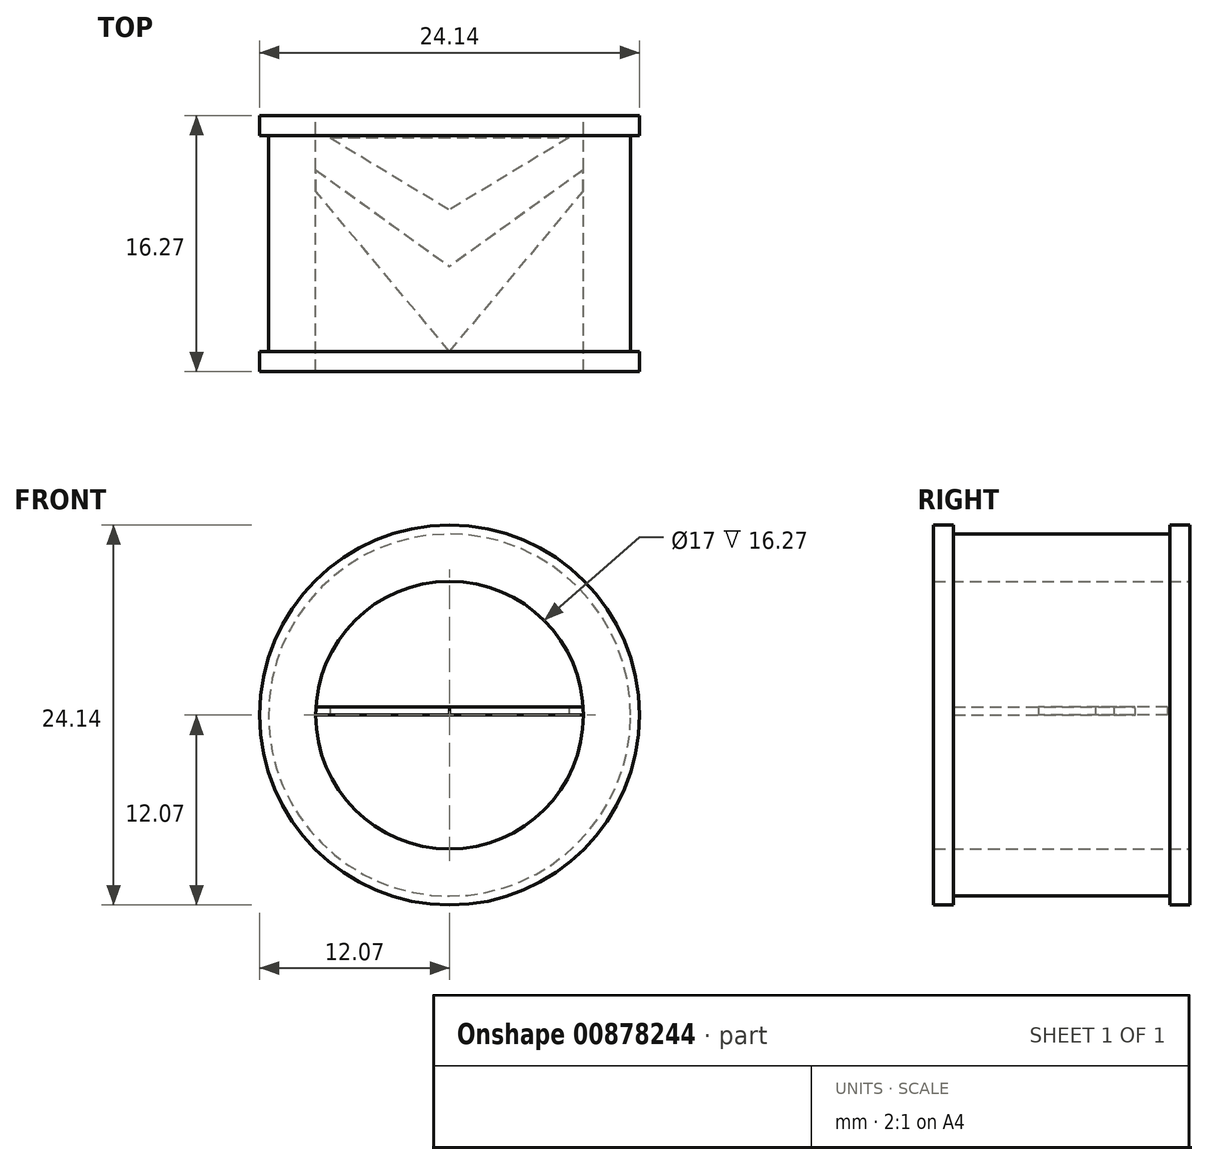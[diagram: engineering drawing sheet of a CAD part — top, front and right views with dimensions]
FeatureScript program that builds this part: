
annotation { "Feature Type Name" : "Feature", "Feature Type Description" : "" }
export const myFeature = defineFeature(function(context is Context, id is Id, definition is map)
    precondition{}
    {
        {
            var Q0;
            Q0=qCreatedBy(makeId("Front.planeOp"),FACE);
            var sketch = newSketch(context, id + "F0", { "sketchPlane" : qUnion([Q0])});
            skCircle(sketch, "E0", {"center": v(0, 0) * mm, "radius": 8.5 * mm});
            skCircle(sketch, "E1", {"center": v(0, 0) * mm, "radius": 11.5 * mm});
            skSolve(sketch);
        }
        {
            var Q0;
            Q0 = qSketchRegion(id + "F0", true);
            extrude(context, id + "F1", {"entities" : qUnion([Q0]), "depth" : 15 * mm, "offsetDistance" : 25.4 * mm});
        }
        {
            var Q0;
            Q0=qCreatedBy(makeId("Front.planeOp"),FACE);
            var sketch = newSketch(context, id + "F2", { "sketchPlane" : qUnion([Q0])});
            skCircle(sketch, "E2", {"center": v(0, 0) * mm, "radius": 12.07 * mm});
            skCircle(sketch, "E3", {"center": v(0, 0) * mm, "radius": 8.57 * mm});
            skSolve(sketch);
        }
        {
            var Q0;
            Q0=makeQuery(id+"F1.opExtrude","CAP_FACE",FACE,{"disambiguationData":[OSD([sQuery(id+"F0.wireOp",EDGE,"E0"),sQuery(id+"F0.wireOp",EDGE,"E1")])],"isStart":false});
            var Q1;
            Q1 = qSketchRegion(id + "F2", true);
            var Q2;
            Q2=sQuery(id+"F2.wireOp",EDGE,"E2");
            extrude(context, id + "F3", {"entities" : qUnion([Q0, Q1]), "operationType" : NewBodyOperationType.ADD, "surfaceOperationType" : NewSurfaceOperationType.ADD, "surfaceEntities" : qUnion([Q2]), "depth" : 1.27 * mm, "offsetDistance" : 25.4 * mm});
        }
        {
            var Q0;
            Q0=makeQuery(id+"F3.opExtrude","CAP_FACE",FACE,{"disambiguationData":[OSD([sQuery(id+"F0.wireOp",EDGE,"E0"),sQuery(id+"F0.wireOp",EDGE,"E1")])],"isStart":false});
            var sketch = newSketch(context, id + "F4", { "sketchPlane" : qUnion([Q0])});
            skCircle(sketch, "E4", {"center": v(0, 0) * mm, "radius": 8.75 * mm});
            skCircle(sketch, "E5", {"center": v(0, 0) * mm, "radius": 12.07 * mm});
            skSolve(sketch);
        }
        {
            var Q0;
            Q0 = qSketchRegion(id + "F4", true);
            extrude(context, id + "F5", {"entities" : qUnion([Q0]), "operationType" : NewBodyOperationType.ADD, "oppositeDirection" : true, "depth" : 1.27 * mm, "offsetDistance" : 25.4 * mm});
        }
        {
            var Q0;
            Q0=qCreatedBy(makeId("Top.planeOp"),FACE);
            var sketch = newSketch(context, id + "F6", { "sketchPlane" : qUnion([Q0])});
            skLineSegment(sketch, "E6", {"start": v(0, -15) * mm, "end": v(-11.34, -1.41) * mm});
            skLineSegment(sketch, "E7", {"start": v(-11.34, -1.41) * mm, "end": v(0, -9.6) * mm});
            skLineSegment(sketch, "E8", {"start": v(0, -1.41) * mm, "end": v(-7.6, -1.41) * mm});
            skLineSegment(sketch, "E9", {"start": v(-7.6, -1.41) * mm, "end": v(0, -6) * mm});
            skLineSegment(sketch, "E10.MirrorCS", {"start": v(0, -1.41) * mm, "end": v(7.6, -1.41) * mm});
            skLineSegment(sketch, "E11.MirrorCS", {"start": v(7.6, -1.41) * mm, "end": v(0, -6) * mm});
            skLineSegment(sketch, "E12.MirrorCS", {"start": v(11.34, -1.41) * mm, "end": v(0, -9.6) * mm});
            skLineSegment(sketch, "E13.MirrorCS", {"start": v(0, -15) * mm, "end": v(11.34, -1.41) * mm});
            skSolve(sketch);
        }
        {
            var Q0;
            Q0 = qSketchRegion(id + "F6", true);
            extrude(context, id + "F7", {"entities" : qUnion([Q0]), "operationType" : NewBodyOperationType.ADD, "depth" : 0.5 * mm, "offsetDistance" : 25.4 * mm});
        }
    });
